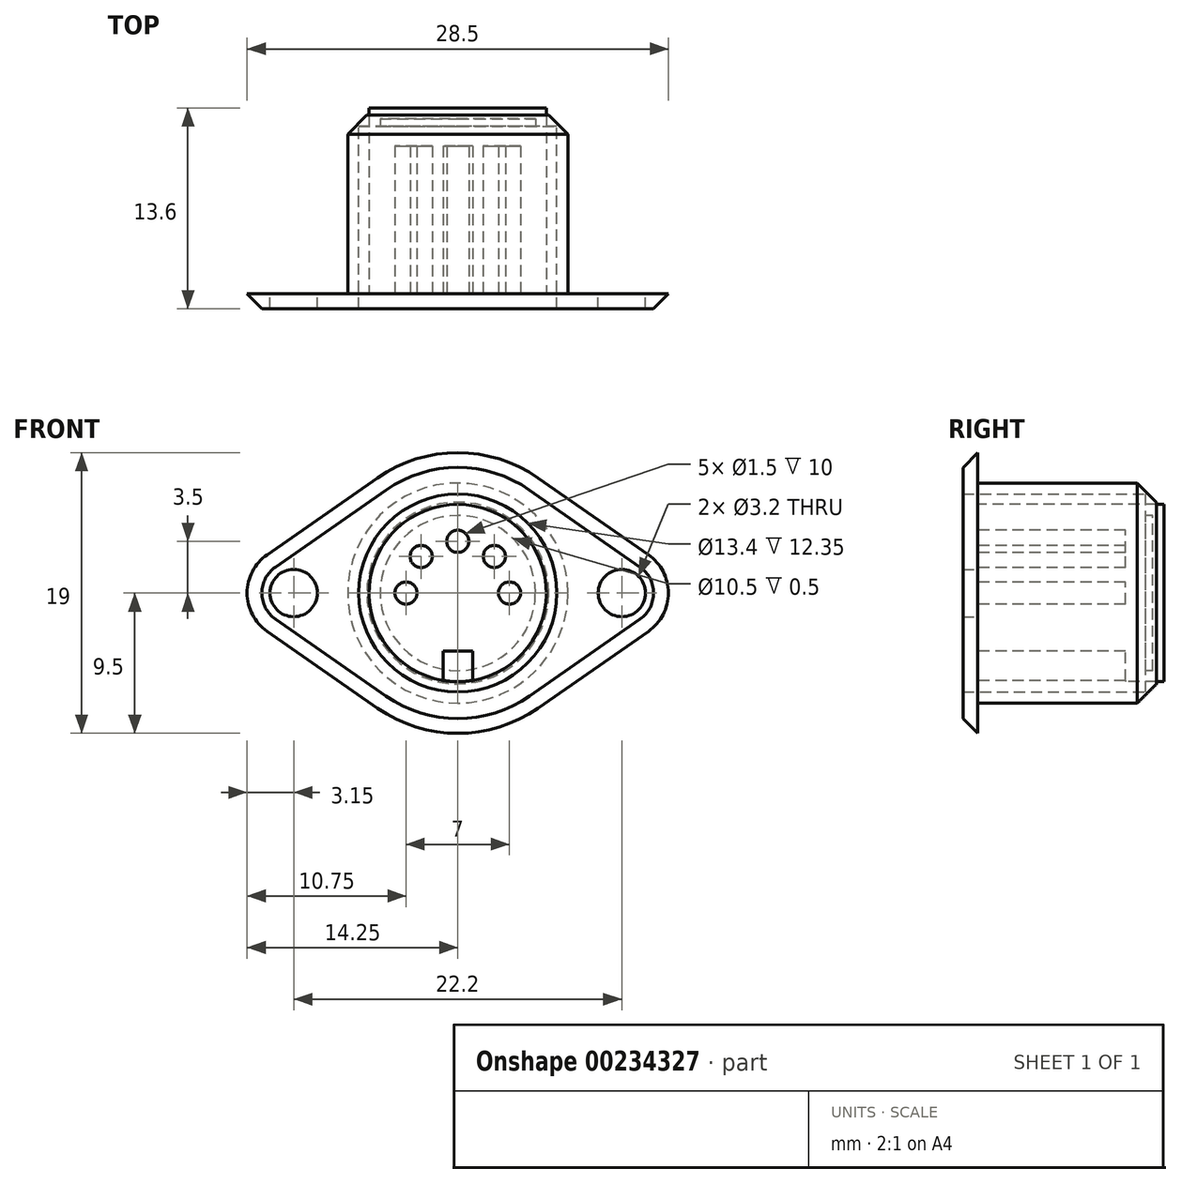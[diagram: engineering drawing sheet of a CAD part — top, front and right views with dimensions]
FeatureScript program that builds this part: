
annotation { "Feature Type Name" : "Feature", "Feature Type Description" : "" }
export const myFeature = defineFeature(function(context is Context, id is Id, definition is map)
    precondition{}
    {
        {
            var Q0;
            Q0=qCreatedBy(makeId("Front.planeOp"),FACE);
            var sketch = newSketch(context, id + "F0", { "sketchPlane" : qUnion([Q0])});
            skCircle(sketch, "E0", {"center": v(-11.1, 0) * mm, "radius": 1.6 * mm});
            skCircle(sketch, "E1", {"center": v(11.1, 0) * mm, "radius": 1.6 * mm});
            skArc(sketch, "E2", {"start": v(-12.9, 2.58) * mm, "mid": v(-14.25, 0) * mm, "end": v(-12.9, -2.58) * mm});
            skLineSegment(sketch, "E3", {"start": v(-14.25, 0) * mm, "end": v(14.25, 0) * mm, "construction": true});
            skCircle(sketch, "E4", {"center": v(0, 0) * mm, "radius": 6 * mm});
            skCircle(sketch, "E5", {"center": v(0, 0) * mm, "radius": 6.7 * mm});
            skArc(sketch, "E6", {"start": v(5.43, 7.8) * mm, "mid": v(0, 9.5) * mm, "end": v(-5.43, 7.8) * mm});
            skLineSegment(sketch, "E7", {"start": v(-12.9, 2.58) * mm, "end": v(-5.43, 7.8) * mm});
            skLineSegment(sketch, "E8", {"start": v(-12.9, -2.58) * mm, "end": v(-5.43, -7.8) * mm});
            skArc(sketch, "E9", {"start": v(12.9, -2.58) * mm, "mid": v(14.25, 0) * mm, "end": v(12.9, 2.58) * mm});
            skLineSegment(sketch, "E10", {"start": v(5.43, 7.8) * mm, "end": v(12.9, 2.58) * mm});
            skLineSegment(sketch, "E11", {"start": v(5.43, -7.8) * mm, "end": v(12.9, -2.58) * mm});
            skArc(sketch, "E12.trimOffspring", {"start": v(-5.43, -7.8) * mm, "mid": v(0, -9.5) * mm, "end": v(5.43, -7.8) * mm});
            skCircle(sketch, "E13", {"center": v(-3.5, 0) * mm, "radius": 0.75 * mm});
            skCircle(sketch, "E14.1.0", {"center": v(-2.47, 2.47) * mm, "radius": 0.75 * mm});
            skCircle(sketch, "E14.2.0", {"center": v(0, 3.5) * mm, "radius": 0.75 * mm});
            skCircle(sketch, "E14.3.0", {"center": v(2.47, 2.47) * mm, "radius": 0.75 * mm});
            skCircle(sketch, "E14.4.0", {"center": v(3.5, 0) * mm, "radius": 0.75 * mm});
            skLineSegment(sketch, "E14.anchor1", {"start": v(0, 0) * mm, "end": v(-3.5, 0) * mm, "construction": true});
            skLineSegment(sketch, "E14.anchor2", {"start": v(0, 0) * mm, "end": v(3.5, 0) * mm, "construction": true});
            skLineSegment(sketch, "E15", {"start": v(-1, -5.92) * mm, "end": v(-1, -3.92) * mm});
            skLineSegment(sketch, "E16", {"start": v(-1, -3.92) * mm, "end": v(0, -3.92) * mm});
            skLineSegment(sketch, "E17.MirrorCS", {"start": v(1, -3.92) * mm, "end": v(0, -3.92) * mm});
            skLineSegment(sketch, "E18.MirrorCS", {"start": v(1, -5.92) * mm, "end": v(1, -3.92) * mm});
            skCircle(sketch, "E19", {"center": v(0, 0) * mm, "radius": 7.45 * mm});
            skLineSegment(sketch, "E20", {"start": v(-1, -5.92) * mm, "end": v(-1, -6.33) * mm});
            skLineSegment(sketch, "E21", {"start": v(-1, -6.33) * mm, "end": v(1, -6.33) * mm});
            skLineSegment(sketch, "E22", {"start": v(1, -6.33) * mm, "end": v(1, -5.92) * mm});
            skSolve(sketch);
        }
        {
            var Q0;
            Q0=makeQuery(id+"F0.imprint","IMPRINT",FACE,{"disambiguationData":[TD([[makeQuery(id+"F0.imprint","IMPRINT",EDGE,{"derivedFrom":sQuery(id+"F0.wireOp",EDGE,"E0")}),-1.0]])]});
            var Q1;
            Q1=makeQuery(id+"F0.imprint","IMPRINT",FACE,{"disambiguationData":[TD([[makeQuery(id+"F0.imprint","IMPRINT",EDGE,{"derivedFrom":sQuery(id+"F0.wireOp",EDGE,"E5")}),-1.0]])]});
            extrude(context, id + "F1", {"entities" : qUnion([Q0, Q1]), "depth" : 1 * mm});
        }
        {
            var Q0;
            Q0=makeQuery(id+"F1.opExtrude","CAP_EDGE",EDGE,{"disambiguationData":[OSD([sQuery(id+"F0.wireOp",EDGE,"E7")])],"isStart":false});
            chamfer(context, id + "F2", {"entities" : qUnion([Q0]), "width" : 1 * mm, "tangentPropagation" : true});
        }
        {
            var Q0;
            Q0=makeQuery(id+"F0.imprint","IMPRINT",FACE,{"disambiguationData":[TD([[makeQuery(id+"F0.imprint","IMPRINT",EDGE,{"derivedFrom":sQuery(id+"F0.wireOp",EDGE,"E5")}),-1.0]])]});
            var Q1;
            Q1=makeQuery(id+"F0.imprint","IMPRINT",FACE,{"disambiguationData":[TD([[makeQuery(id+"F0.imprint","IMPRINT",EDGE,{"derivedFrom":sQuery(id+"F0.wireOp",EDGE,"E5")}),1.0]])]});
            var Q2;
            Q2=makeQuery(id+"F0.imprint","IMPRINT",FACE,{"disambiguationData":[TD([[makeQuery(id+"F0.imprint","IMPRINT",EDGE,{"derivedFrom":sQuery(id+"F0.wireOp",EDGE,"E13")}),-1.0]])]});
            var Q3;
            Q3=makeQuery(id+"F0.imprint","IMPRINT",FACE,{"disambiguationData":[TD([[makeQuery(id+"F0.imprint","IMPRINT",EDGE,{"derivedFrom":sQuery(id+"F0.wireOp",EDGE,"E13")}),1.0]])]});
            var Q4;
            Q4=makeQuery(id+"F0.imprint","IMPRINT",FACE,{"disambiguationData":[TD([[makeQuery(id+"F0.imprint","IMPRINT",EDGE,{"derivedFrom":sQuery(id+"F0.wireOp",EDGE,"E14.1.0")}),1.0]])]});
            var Q5;
            Q5=makeQuery(id+"F0.imprint","IMPRINT",FACE,{"disambiguationData":[TD([[makeQuery(id+"F0.imprint","IMPRINT",EDGE,{"derivedFrom":sQuery(id+"F0.wireOp",EDGE,"E14.2.0")}),1.0]])]});
            var Q6;
            Q6=makeQuery(id+"F0.imprint","IMPRINT",FACE,{"disambiguationData":[TD([[makeQuery(id+"F0.imprint","IMPRINT",EDGE,{"derivedFrom":sQuery(id+"F0.wireOp",EDGE,"E14.3.0")}),1.0]])]});
            var Q7;
            Q7=makeQuery(id+"F0.imprint","IMPRINT",FACE,{"disambiguationData":[TD([[makeQuery(id+"F0.imprint","IMPRINT",EDGE,{"derivedFrom":sQuery(id+"F0.wireOp",EDGE,"E14.4.0")}),1.0]])]});
            var Q8;
            {var subQ0=sQuery(id+"F0.wireOp",EDGE,"E15");Q8=makeQuery(id+"F0.imprint","IMPRINT",FACE,{"disambiguationData":[TD([[makeQuery(id+"F0.imprint","IMPRINT",EDGE,{"derivedFrom":subQ0}),-1.0]])]});}
            var Q9;
            {var subQ0=sQuery(id+"F0.wireOp",EDGE,"E20");Q9=makeQuery(id+"F0.imprint","IMPRINT",FACE,{"disambiguationData":[TD([[makeQuery(id+"F0.imprint","IMPRINT",EDGE,{"derivedFrom":subQ0}),1.0]])]});}
            var Q10;
            Q10=sQuery(id+"F0.wireOp",EDGE,"E5");
            extrude(context, id + "F3", {"entities" : qUnion([Q0, Q1, Q2, Q3, Q4, Q5, Q6, Q7, Q8, Q9]), "operationType" : NewBodyOperationType.ADD, "surfaceEntities" : qUnion([Q10]), "oppositeDirection" : true, "depth" : 12.1 * mm});
        }
        {
            var Q0;
            Q0=makeQuery(id+"F3.opExtrude","CAP_FACE",FACE,{"disambiguationData":[OSD([sQuery(id+"F0.wireOp",EDGE,"E19")])],"isStart":true});
            shell(context, id + "F4", {"entities" : qUnion([Q0]), "thickness" : .75 * mm});
        }
        {
            var Q0;
            Q0=makeQuery(id+"F0.imprint","IMPRINT",FACE,{"disambiguationData":[TD([[makeQuery(id+"F0.imprint","IMPRINT",EDGE,{"derivedFrom":sQuery(id+"F0.wireOp",EDGE,"E13")}),-1.0]])]});
            var Q1;
            Q1=makeQuery(id+"F0.imprint","IMPRINT",FACE,{"disambiguationData":[TD([[makeQuery(id+"F0.imprint","IMPRINT",EDGE,{"derivedFrom":sQuery(id+"F0.wireOp",EDGE,"E13")}),1.0]])]});
            var Q2;
            Q2=makeQuery(id+"F0.imprint","IMPRINT",FACE,{"disambiguationData":[TD([[makeQuery(id+"F0.imprint","IMPRINT",EDGE,{"derivedFrom":sQuery(id+"F0.wireOp",EDGE,"E14.1.0")}),1.0]])]});
            var Q3;
            Q3=makeQuery(id+"F0.imprint","IMPRINT",FACE,{"disambiguationData":[TD([[makeQuery(id+"F0.imprint","IMPRINT",EDGE,{"derivedFrom":sQuery(id+"F0.wireOp",EDGE,"E14.2.0")}),1.0]])]});
            var Q4;
            Q4=makeQuery(id+"F0.imprint","IMPRINT",FACE,{"disambiguationData":[TD([[makeQuery(id+"F0.imprint","IMPRINT",EDGE,{"derivedFrom":sQuery(id+"F0.wireOp",EDGE,"E14.3.0")}),1.0]])]});
            var Q5;
            Q5=makeQuery(id+"F0.imprint","IMPRINT",FACE,{"disambiguationData":[TD([[makeQuery(id+"F0.imprint","IMPRINT",EDGE,{"derivedFrom":sQuery(id+"F0.wireOp",EDGE,"E14.4.0")}),1.0]])]});
            var Q6;
            {var subQ0=sQuery(id+"F0.wireOp",EDGE,"E15");Q6=makeQuery(id+"F0.imprint","IMPRINT",FACE,{"disambiguationData":[TD([[makeQuery(id+"F0.imprint","IMPRINT",EDGE,{"derivedFrom":subQ0}),-1.0]])]});}
            extrude(context, id + "F5", {"entities" : qUnion([Q0, Q1, Q2, Q3, Q4, Q5, Q6]), "oppositeDirection" : true, "depth" : 12.6 * mm});
        }
        {
            var Q0;
            Q0=makeQuery(id+"F0.imprint","IMPRINT",FACE,{"disambiguationData":[TD([[makeQuery(id+"F0.imprint","IMPRINT",EDGE,{"derivedFrom":sQuery(id+"F0.wireOp",EDGE,"E13")}),1.0]])]});
            var Q1;
            {var subQ0=sQuery(id+"F0.wireOp",EDGE,"E15");Q1=makeQuery(id+"F0.imprint","IMPRINT",FACE,{"disambiguationData":[TD([[makeQuery(id+"F0.imprint","IMPRINT",EDGE,{"derivedFrom":subQ0}),-1.0]])]});}
            var Q2;
            Q2=makeQuery(id+"F0.imprint","IMPRINT",FACE,{"disambiguationData":[TD([[makeQuery(id+"F0.imprint","IMPRINT",EDGE,{"derivedFrom":sQuery(id+"F0.wireOp",EDGE,"E14.1.0")}),1.0]])]});
            var Q3;
            Q3=makeQuery(id+"F0.imprint","IMPRINT",FACE,{"disambiguationData":[TD([[makeQuery(id+"F0.imprint","IMPRINT",EDGE,{"derivedFrom":sQuery(id+"F0.wireOp",EDGE,"E14.2.0")}),1.0]])]});
            var Q4;
            Q4=makeQuery(id+"F0.imprint","IMPRINT",FACE,{"disambiguationData":[TD([[makeQuery(id+"F0.imprint","IMPRINT",EDGE,{"derivedFrom":sQuery(id+"F0.wireOp",EDGE,"E14.3.0")}),1.0]])]});
            var Q5;
            Q5=makeQuery(id+"F0.imprint","IMPRINT",FACE,{"disambiguationData":[TD([[makeQuery(id+"F0.imprint","IMPRINT",EDGE,{"derivedFrom":sQuery(id+"F0.wireOp",EDGE,"E14.4.0")}),1.0]])]});
            extrude(context, id + "F6", {"entities" : qUnion([Q0, Q1, Q2, Q3, Q4, Q5]), "operationType" : NewBodyOperationType.REMOVE, "oppositeDirection" : true, "depth" : 10 * mm});
        }
        {
            var Q0;
            Q0=makeQuery(id+"F3.opExtrude","CAP_EDGE",EDGE,{"disambiguationData":[OSD([sQuery(id+"F0.wireOp",EDGE,"E19")])],"isStart":false});
            chamfer(context, id + "F7", {"entities" : qUnion([Q0]), "width" : 1.3 * mm, "tangentPropagation" : true});
        }
    });
